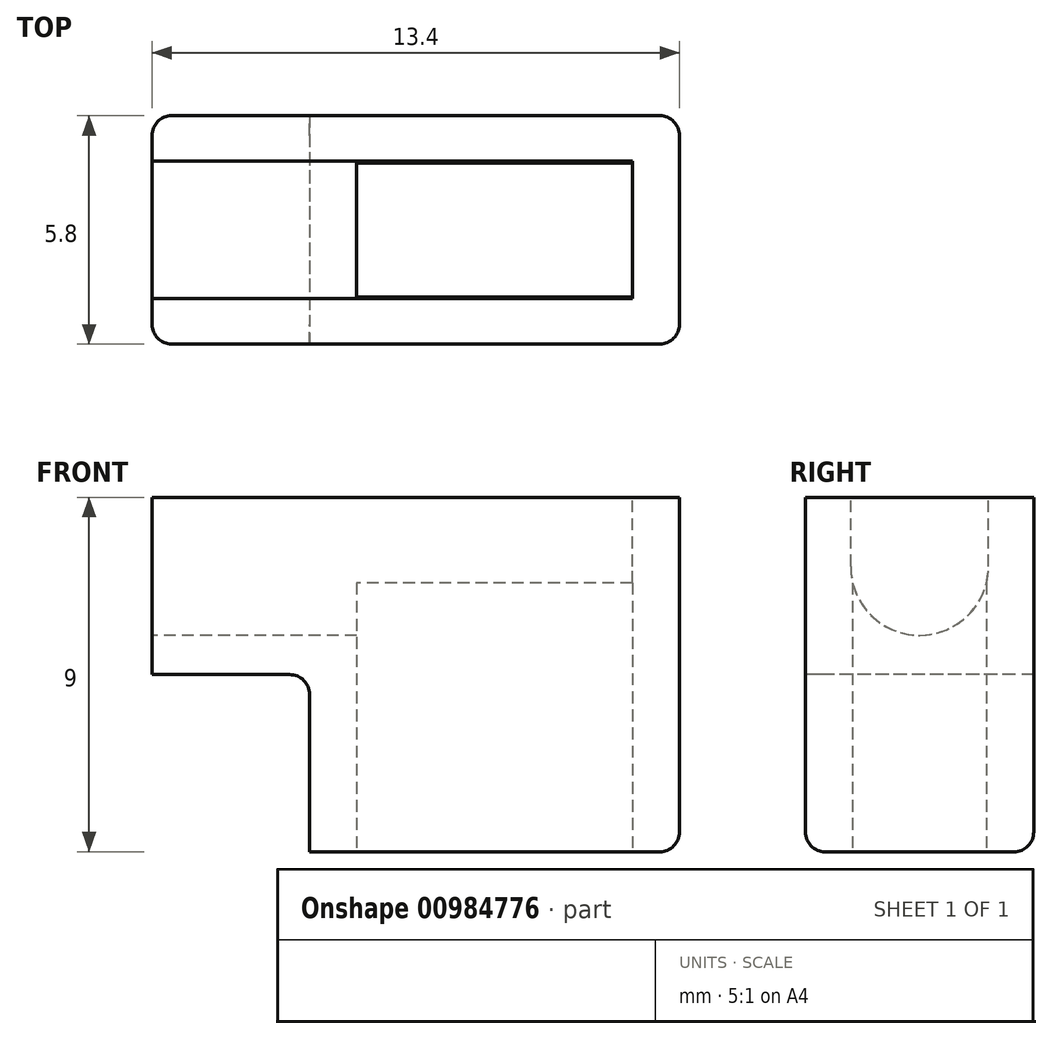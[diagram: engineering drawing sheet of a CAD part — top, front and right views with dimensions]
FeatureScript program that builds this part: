
annotation { "Feature Type Name" : "Feature", "Feature Type Description" : "" }
export const myFeature = defineFeature(function(context is Context, id is Id, definition is map)
    precondition{}
    {
        {
            var Q0;
            Q0=qCreatedBy(makeId("Top.planeOp"),FACE);
            var sketch = newSketch(context, id + "F0", { "sketchPlane" : qUnion([Q0])});
            skLineSegment(sketch, "E0.bottom", {"start": v(3.5, 1.7) * mm, "end": v(-3.5, 1.7) * mm});
            skLineSegment(sketch, "E0.top", {"start": v(3.5, -1.7) * mm, "end": v(-3.5, -1.7) * mm});
            skLineSegment(sketch, "E0.left", {"start": v(3.5, 1.7) * mm, "end": v(3.5, -1.7) * mm});
            skLineSegment(sketch, "E0.right", {"start": v(-3.5, 1.7) * mm, "end": v(-3.5, -1.7) * mm});
            skPoint(sketch, "E0.middle", {"position": v(0, 0) * mm});
            skLineSegment(sketch, "E1.0", {"start": v(4.7, 2.9) * mm, "end": v(-4.7, 2.9) * mm});
            skLineSegment(sketch, "E1.1", {"start": v(4.7, 2.9) * mm, "end": v(4.7, -2.9) * mm});
            skLineSegment(sketch, "E1.2", {"start": v(4.7, -2.9) * mm, "end": v(-4.7, -2.9) * mm});
            skLineSegment(sketch, "E1.3", {"start": v(-4.7, 2.9) * mm, "end": v(-4.7, -2.9) * mm});
            skLineSegment(sketch, "E2.bottom", {"start": v(-4.7, 2.9) * mm, "end": v(-8.7, 2.9) * mm});
            skLineSegment(sketch, "E2.top", {"start": v(-4.7, -2.9) * mm, "end": v(-8.7, -2.9) * mm});
            skLineSegment(sketch, "E2.right", {"start": v(-8.7, 2.9) * mm, "end": v(-8.7, -2.9) * mm});
            skSolve(sketch);
        }
        {
            var Q0;
            Q0=makeQuery(id+"F0.imprint","IMPRINT",FACE,{"disambiguationData":[TD([[makeQuery(id+"F0.imprint","IMPRINT",EDGE,{"derivedFrom":sQuery(id+"F0.wireOp",EDGE,"E2.bottom")}),1.0]])]});
            var Q1;
            Q1=makeQuery(id+"F0.imprint","IMPRINT",FACE,{"disambiguationData":[TD([[makeQuery(id+"F0.imprint","IMPRINT",EDGE,{"derivedFrom":sQuery(id+"F0.wireOp",EDGE,"E0.bottom")}),-1.0]])]});
            extrude(context, id + "F1", {"entities" : qUnion([Q0, Q1]), "depth" : 9 * mm, "offsetDistance" : 25 * mm});
        }
        {
            var Q0;
            Q0=makeQuery(id+"F0.imprint","IMPRINT",FACE,{"disambiguationData":[TD([[makeQuery(id+"F0.imprint","IMPRINT",EDGE,{"derivedFrom":sQuery(id+"F0.wireOp",EDGE,"E2.bottom")}),1.0]])]});
            extrude(context, id + "F2", {"entities" : qUnion([Q0]), "operationType" : NewBodyOperationType.REMOVE, "depth" : 4.5 * mm, "offsetDistance" : 25 * mm});
        }
        {
            var Q0;
            Q0=makeQuery(id+"F1.opExtrude","SWEPT_FACE",FACE,{"disambiguationData":[OSD([sQuery(id+"F0.wireOp",EDGE,"E2.right")])]});
            var sketch = newSketch(context, id + "F3", { "sketchPlane" : qUnion([Q0])});
            skArc(sketch, "E3", {"start": v(-1.75, 7.25) * mm, "mid": v(0, 5.5) * mm, "end": v(1.75, 7.25) * mm});
            skLineSegment(sketch, "E4", {"start": v(-1.75, 7.25) * mm, "end": v(-1.75, 9) * mm});
            skLineSegment(sketch, "E5", {"start": v(1.75, 7.25) * mm, "end": v(1.75, 9) * mm});
            skLineSegment(sketch, "E6", {"start": v(-1.75, 9) * mm, "end": v(1.75, 9) * mm});
            skSolve(sketch);
        }
        {
            var Q0;
            Q0 = qSketchRegion(id + "F3", true);
            var Q1;
            Q1=makeQuery(id+"F1.opExtrude","SWEPT_FACE",FACE,{"disambiguationData":[OSD([sQuery(id+"F0.wireOp",EDGE,"E0.left")])]});
            extrude(context, id + "F4", {"entities" : qUnion([Q0]), "operationType" : NewBodyOperationType.REMOVE, "endBound" : BoundingType.UP_TO_SURFACE, "oppositeDirection" : true, "depth" : 25 * mm, "endBoundEntityFace" : qUnion([Q1]), "offsetDistance" : 25 * mm});
        }
        {
            var Q0;
            Q0=makeQuery(id+"F2.boolean.opBoolean","COPY",EDGE,{"derivedFrom":makeQuery(id+"F2.opExtrude","SWEPT_EDGE",EDGE,{"disambiguationData":[OSD([sQuery(id+"F0.wireOp",EDGE,"E1.0"),sQuery(id+"F0.wireOp",EDGE,"E2.bottom"),sQuery(id+"F0.wireOp",EDGE,"E1.3")])]})});
            var Q1;
            Q1=makeQuery(id+"F2.boolean.opBoolean","COPY",EDGE,{"derivedFrom":makeQuery(id+"F2.opExtrude","CAP_EDGE",EDGE,{"disambiguationData":[OSD([sQuery(id+"F0.wireOp",EDGE,"E2.bottom")])],"isStart":false})});
            var Q2;
            Q2=makeQuery(id+"F2.boolean.opBoolean","COPY",EDGE,{"derivedFrom":makeQuery(id+"F2.opExtrude","CAP_EDGE",EDGE,{"disambiguationData":[OSD([sQuery(id+"F0.wireOp",EDGE,"E1.3")])],"isStart":false})});
            var Q3;
            Q3=makeQuery(id+"F2.boolean.opBoolean","COPY",EDGE,{"derivedFrom":makeQuery(id+"F2.opExtrude","SWEPT_EDGE",EDGE,{"disambiguationData":[OSD([sQuery(id+"F0.wireOp",EDGE,"E1.2"),sQuery(id+"F0.wireOp",EDGE,"E2.top"),sQuery(id+"F0.wireOp",EDGE,"E1.3")])]})});
            var Q4;
            Q4=makeQuery(id+"F1.opExtrude","SWEPT_EDGE",EDGE,{"disambiguationData":[OSD([sQuery(id+"F0.wireOp",EDGE,"E1.1"),sQuery(id+"F0.wireOp",EDGE,"E1.2")])]});
            var Q5;
            Q5=makeQuery(id+"F1.opExtrude","SWEPT_EDGE",EDGE,{"disambiguationData":[OSD([sQuery(id+"F0.wireOp",EDGE,"E1.0"),sQuery(id+"F0.wireOp",EDGE,"E1.1")])]});
            var Q6;
            Q6=makeQuery(id+"F1.opExtrude","CAP_EDGE",EDGE,{"disambiguationData":[OSD([sQuery(id+"F0.wireOp",EDGE,"E1.0"),sQuery(id+"F0.wireOp",EDGE,"E2.bottom")])],"isStart":true});
            var Q7;
            Q7=makeQuery(id+"F1.opExtrude","CAP_EDGE",EDGE,{"disambiguationData":[OSD([sQuery(id+"F0.wireOp",EDGE,"E1.1")])],"isStart":true});
            var Q8;
            Q8=makeQuery(id+"F1.opExtrude","CAP_EDGE",EDGE,{"disambiguationData":[OSD([sQuery(id+"F0.wireOp",EDGE,"E1.2"),sQuery(id+"F0.wireOp",EDGE,"E2.top")])],"isStart":true});
            var Q9;
            Q9=makeQuery(id+"F2.boolean.opBoolean","COPY",EDGE,{"derivedFrom":makeQuery(id+"F2.opExtrude","CAP_EDGE",EDGE,{"disambiguationData":[OSD([sQuery(id+"F0.wireOp",EDGE,"E1.3")])],"isStart":true})});
            var Q10;
            Q10=makeQuery(id+"F1.opExtrude","SWEPT_EDGE",EDGE,{"disambiguationData":[OSD([sQuery(id+"F0.wireOp",EDGE,"E2.bottom"),sQuery(id+"F0.wireOp",EDGE,"E2.right")])]});
            var Q11;
            Q11=makeQuery(id+"F2.boolean.opBoolean","COPY",EDGE,{"derivedFrom":makeQuery(id+"F2.opExtrude","CAP_EDGE",EDGE,{"disambiguationData":[OSD([sQuery(id+"F0.wireOp",EDGE,"E2.right")])],"isStart":false})});
            var Q12;
            Q12=makeQuery(id+"F1.opExtrude","SWEPT_EDGE",EDGE,{"disambiguationData":[OSD([sQuery(id+"F0.wireOp",EDGE,"E2.top"),sQuery(id+"F0.wireOp",EDGE,"E2.right")])]});
            var Q13;
            Q13=makeQuery(id+"F4.boolean.opBoolean","COPY",EDGE,{"derivedFrom":makeQuery(id+"F4.opExtrude","CAP_EDGE",EDGE,{"disambiguationData":[OSD([sQuery(id+"F3.wireOp",EDGE,"E3")])],"isStart":true})});
            fillet(context, id + "F5", {"entities" : qUnion([Q0, Q1, Q2, Q3, Q4, Q5, Q6, Q7, Q8, Q9, Q10, Q11, Q12, Q13]), "radius" : 0.5 * mm, "tangentPropagation" : true, "allowEdgeOverflow" : false});
        }
    });
